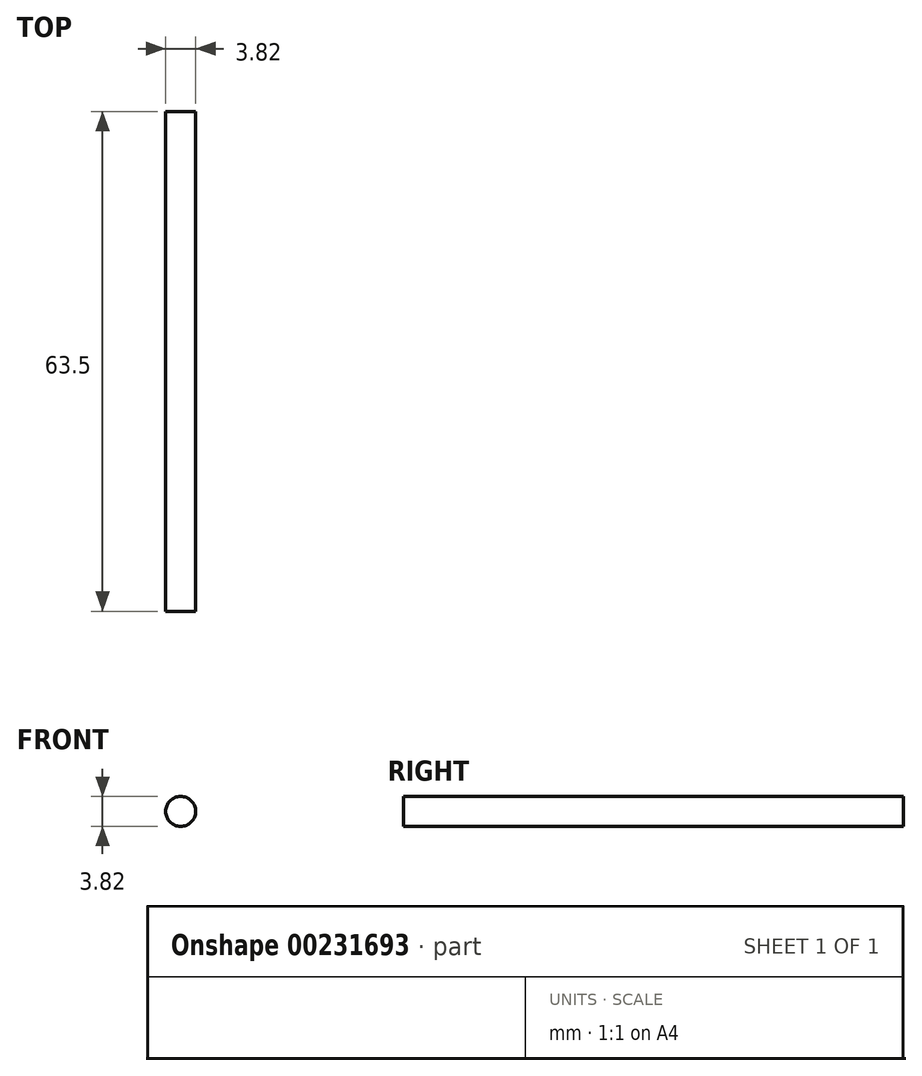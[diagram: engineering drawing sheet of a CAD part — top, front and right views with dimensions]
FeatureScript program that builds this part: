
annotation { "Feature Type Name" : "Feature", "Feature Type Description" : "" }
export const myFeature = defineFeature(function(context is Context, id is Id, definition is map)
    precondition{}
    {
        {
            var Q0;
            Q0=qCreatedBy(makeId("Front.planeOp"),FACE);
            var sketch = newSketch(context, id + "F0", { "sketchPlane" : qUnion([Q0])});
            skCircle(sketch, "E0", {"center": v(0, 0) * mm, "radius": 1.9 * mm});
            skSolve(sketch);
        }
        {
            var Q0;
            Q0=makeQuery(id+"F0.imprint","IMPRINT",FACE,{"disambiguationData":[TD([[makeQuery(id+"F0.imprint","IMPRINT",EDGE,{"derivedFrom":sQuery(id+"F0.wireOp",EDGE,"E0")}),1.0]])]});
            extrude(context, id + "F1", {"entities" : qUnion([Q0]), "depth" : 63.5 * mm});
        }
    });
